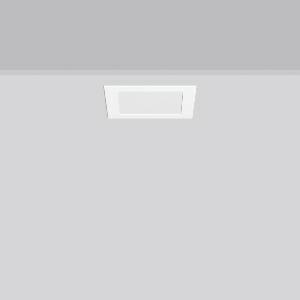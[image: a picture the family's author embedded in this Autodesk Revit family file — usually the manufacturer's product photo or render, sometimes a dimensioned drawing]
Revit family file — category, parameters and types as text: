
# Revit family: toledo_flat_square_e_901486_002_023f
name_source: partatom
category: Lighting Fixtures
units: mm (PartAtom-declared; Revit-internal decimal feet)

## family parameters
Cut with Voids When Loaded = No
Host = Face
Light Source = No
Part Type = Normal
Room Calculation Point = No
Round Connector Dimension = Use Diameter
Shared = No

## types (1)
- TOLEDO FLAT square E (1 x LED Modul 830, 770 lm, 3000)
    Apparent Load = 8 VA
    CIE Flux Codes = 49 80 96 100 100
    Color Rendering = 80
    Color Temperature = 3000
    Default Elevation = 1800 mm
    Description = Series: TOLEDO FLAT square
Ultra thin recessed downlight. Housing: die-cast aluminium. Light guide and diffuser made of non-yellowing PMMA, opal matt. Ceiling installation with spring system. Mounting depth depends on ceiling strength. Suitable for through-wiring with separately available accessories. Surface mounted housing as accessory for all sizes. Retrofittable decorative cylinders made of chintz fabric as accessory, optional with satin finish plastic diffuser. Through-wiring box (5 pole) available as accessory. 
Colour: white
Length: 172 mm
Width: 172 mm
Height: 3 mm
Cut-out length: 156 mm
Cut-out width: 156 mm
Recess height: 28-56 mm
Luminaire: recess height: 31-51 mm
Lamp: LED
Socket: without socket
Colour temperature: 3000K
Colour rendering index (CRI): 80
System power: 8 W
Rated luminous flux: 770 lm
Luminous efficiency: 96 lm/W
Control gear: Regulated power supply
Protection class: II
Type of protection: IP 54
    Height = 0 mm  [stored 0 ft]
    Lamp = 1 x LED Modul 830
    Lamp Light Flux = 770 lm
    Lamp count = 1
    Length = 172 mm
    Lifetime = 50000 h
    Luminous efficacy = 96 lm/W
    Manufacturer = RZB
    ModVariant = No
    Model = 901486.002
    Mounting Place = Ceiling
    Mounting Type = Recessed
    Number of Poles = 1
    OnlyDefault = Yes
    Power Factor = 1
    Product Name = TOLEDO FLAT square E
    Product group = Recessed downlights
    ProductGroupID = 402
    Protection Class = Protection class II
    Protection Degree = IP 20
    RLX_Detail_Level = 1
    RLX_Emergency_Light_Flux = 0 lm
    RLX_Emergency_Type = 0
    RLX_Emergency_Type_DB = No
    RlxData = <blob elided: 57801 chars, md5=7671ac46>
    Socket = socket
    Standby Power = 0 W
    System Light Flux = 770 lm
    System Power = 8 W
    Type Comments = Product without accessories
    Type Image = 901486.002.jpg
    URL = http://relux.com
    VarID = ---
    Voltage = 230 V
    Voltage Range = 220-240 V
    Weight = 0.00 kg
    Width = 172 mm

note: [stored X ft] marks values corroborated as IEEE doubles in the binary element streams (Revit-internal decimal feet)

## geometry (parser evidence)
native form markers: Blend x4, Sweep x9
no freeform markers — native parametric forms only
